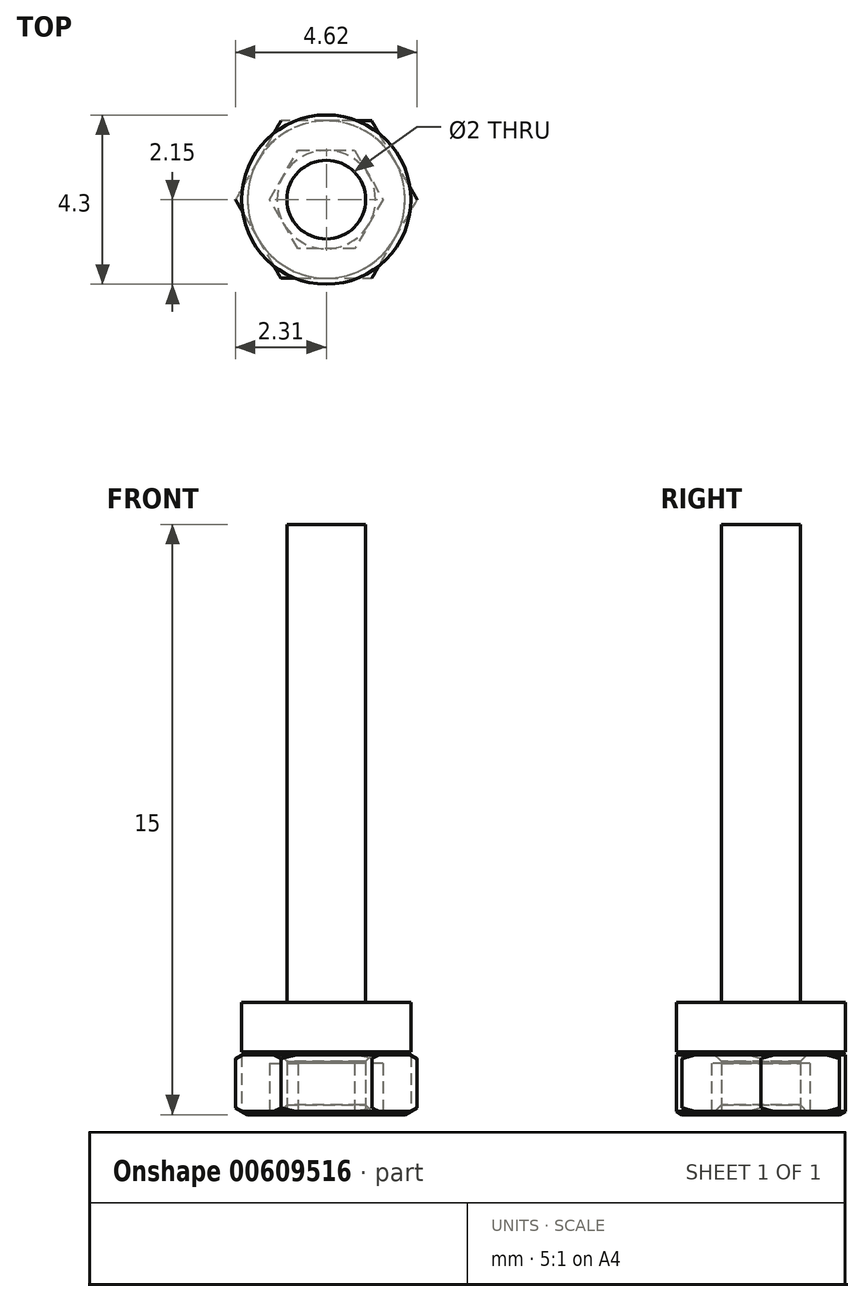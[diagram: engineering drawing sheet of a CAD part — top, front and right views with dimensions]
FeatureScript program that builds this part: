
annotation { "Feature Type Name" : "Feature", "Feature Type Description" : "" }
export const myFeature = defineFeature(function(context is Context, id is Id, definition is map)
    precondition{}
    {
        {
            var Q0;
            Q0=qCreatedBy(makeId("Top.planeOp"),FACE);
            var sketch = newSketch(context, id + "F0", { "sketchPlane" : qUnion([Q0])});
            skCircle(sketch, "E0", {"center": v(0, 0) * mm, "radius": 2.15 * mm});
            skCircle(sketch, "E1", {"center": v(0, 0) * mm, "radius": 1 * mm});
            skSolve(sketch);
        }
        {
            var Q0;
            Q0=makeQuery(id+"F0.imprint","IMPRINT",FACE,{"disambiguationData":[TD([[makeQuery(id+"F0.imprint","IMPRINT",EDGE,{"derivedFrom":sQuery(id+"F0.wireOp",EDGE,"E1")}),1.0]])]});
            var Q1;
            Q1=makeQuery(id+"F0.imprint","IMPRINT",FACE,{"disambiguationData":[TD([[makeQuery(id+"F0.imprint","IMPRINT",EDGE,{"derivedFrom":sQuery(id+"F0.wireOp",EDGE,"E0")}),1.0]])]});
            extrude(context, id + "F1", {"entities" : qUnion([Q0, Q1]), "depth" : 2.85 * mm});
        }
        {
            var Q0;
            Q0=makeQuery(id+"F0.imprint","IMPRINT",FACE,{"disambiguationData":[TD([[makeQuery(id+"F0.imprint","IMPRINT",EDGE,{"derivedFrom":sQuery(id+"F0.wireOp",EDGE,"E1")}),1.0]])]});
            extrude(context, id + "F2", {"entities" : qUnion([Q0]), "operationType" : NewBodyOperationType.ADD, "depth" : 15 * mm});
        }
        {
            var Q0;
            Q0=makeQuery(id+"F0.imprint","IMPRINT",FACE,{"disambiguationData":[TD([[makeQuery(id+"F0.imprint","IMPRINT",EDGE,{"derivedFrom":sQuery(id+"F0.wireOp",EDGE,"E0")}),1.0]])]});
            var sketch = newSketch(context, id + "F3", { "sketchPlane" : qUnion([Q0])});
            skCircle(sketch, "E2.cCircle", {"center": v(0, 0) * mm, "radius": 1.25 * mm, "construction": true});
            skLineSegment(sketch, "E2.0", {"start": v(0.72, -1.25) * mm, "end": v(-0.72, -1.25) * mm});
            skLineSegment(sketch, "E2.1", {"start": v(-0.72, -1.25) * mm, "end": v(-1.44, 0) * mm});
            skLineSegment(sketch, "E2.2", {"start": v(-1.44, 0) * mm, "end": v(-0.72, 1.25) * mm});
            skLineSegment(sketch, "E2.3", {"start": v(-0.72, 1.25) * mm, "end": v(0.72, 1.25) * mm});
            skLineSegment(sketch, "E2.4", {"start": v(0.72, 1.25) * mm, "end": v(1.44, 0) * mm});
            skLineSegment(sketch, "E2.5", {"start": v(1.44, 0) * mm, "end": v(0.72, -1.25) * mm});
            skPoint(sketch, "E2.0.midPoint", {"position": v(0, -1.25) * mm});
            skSolve(sketch);
        }
        {
            var Q0;
            Q0=makeQuery(id+"F3.imprint","IMPRINT",FACE,{"disambiguationData":[TD([[makeQuery(id+"F3.imprint","IMPRINT",EDGE,{"derivedFrom":sQuery(id+"F3.wireOp",EDGE,"E2.0")}),-1.0]])]});
            extrude(context, id + "F4", {"entities" : qUnion([Q0]), "operationType" : NewBodyOperationType.REMOVE, "depth" : 1.3 * mm});
        }
        {
            var Q0;
            Q0=qCreatedBy(makeId("Top.planeOp"),FACE);
            var sketch = newSketch(context, id + "F5", { "sketchPlane" : qUnion([Q0])});
            skCircle(sketch, "E3", {"center": v(0, 0) * mm, "radius": 1 * mm});
            skLineSegment(sketch, "E4.0", {"start": v(2, 1.06) * mm, "end": v(2, -1.06) * mm});
            skPoint(sketch, "E4.0.midPoint", {"position": v(2, 0) * mm});
            skCircle(sketch, "E5.cCircle", {"center": v(0, 0) * mm, "radius": 2 * mm, "construction": true});
            skLineSegment(sketch, "E5.0", {"start": v(2, 1.15) * mm, "end": v(2, -1.15) * mm});
            skLineSegment(sketch, "E5.1", {"start": v(2, -1.15) * mm, "end": v(0, -2.3) * mm});
            skLineSegment(sketch, "E5.2", {"start": v(0, -2.3) * mm, "end": v(-2, -1.15) * mm});
            skLineSegment(sketch, "E5.3", {"start": v(-2, -1.15) * mm, "end": v(-2, 1.15) * mm});
            skLineSegment(sketch, "E5.4", {"start": v(-2, 1.15) * mm, "end": v(0, 2.3) * mm});
            skLineSegment(sketch, "E5.5", {"start": v(0, 2.3) * mm, "end": v(2, 1.15) * mm});
            skSolve(sketch);
        }
        {
            var Q0;
            Q0=makeQuery(id+"F5.imprint","IMPRINT",FACE,{"disambiguationData":[TD([[makeQuery(id+"F5.imprint","IMPRINT",EDGE,{"derivedFrom":sQuery(id+"F5.wireOp",EDGE,"E3")}),-1.0]])]});
            extrude(context, id + "F6", {"entities" : qUnion([Q0]), "depth" : 1.6 * mm, "offsetDistance" : 25 * mm});
        }
        {
            var Q0;
            Q0=qCreatedBy(makeId("Front.planeOp"),FACE);
            var sketch = newSketch(context, id + "F7", { "sketchPlane" : qUnion([Q0])});
            skLineSegment(sketch, "E6", {"start": v(0, 0) * mm, "end": v(0, 1.6) * mm, "construction": true});
            skLineSegment(sketch, "E7", {"start": v(0, 0.8) * mm, "end": v(3.39, 0.8) * mm, "construction": true});
            skPoint(sketch, "E7.endSnap0", {"position": v(0, 0.8) * mm});
            skLineSegment(sketch, "E8", {"start": v(2, 1.6) * mm, "end": v(3.39, 1.6) * mm});
            skLineSegment(sketch, "E9", {"start": v(3.39, 1.6) * mm, "end": v(3.39, 0.8) * mm});
            skLineSegment(sketch, "E10", {"start": v(3.39, 0.8) * mm, "end": v(2, 1.6) * mm});
            skLineSegment(sketch, "E11.MirrorCS", {"start": v(2, 0) * mm, "end": v(3.39, 0) * mm});
            skLineSegment(sketch, "E12.MirrorCS", {"start": v(3.39, 0) * mm, "end": v(3.39, 0.8) * mm});
            skLineSegment(sketch, "E13.MirrorCS", {"start": v(3.39, 0.8) * mm, "end": v(2, 0) * mm});
            skSolve(sketch);
        }
        {
            var Q0;
            Q0=makeQuery(id+"F7.imprint","IMPRINT",FACE,{"disambiguationData":[TD([[makeQuery(id+"F7.imprint","IMPRINT",EDGE,{"derivedFrom":sQuery(id+"F7.wireOp",EDGE,"E8")}),-1.0]])]});
            var Q1;
            Q1=makeQuery(id+"F7.imprint","IMPRINT",FACE,{"disambiguationData":[TD([[makeQuery(id+"F7.imprint","IMPRINT",EDGE,{"derivedFrom":sQuery(id+"F7.wireOp",EDGE,"E11.MirrorCS")}),1.0]])]});
            var Q2;
            Q2=sQuery(id+"F7.wireOp",EDGE,"E6");
            revolve(context, id + "F8", {"operationType" : NewBodyOperationType.REMOVE, "entities" : qUnion([Q0, Q1]), "axis" : qUnion([Q2]), "revolveType" : RevolveType.FULL, "oppositeDirection" : true});
        }
        {
            var Q0;
            Q0=makeQuery(id+"F6.opExtrude","SWEPT_FACE",FACE,{"disambiguationData":[OSD([sQuery(id+"F5.wireOp",EDGE,"E3")])]});
            chamfer(context, id + "F9", {"entities" : qUnion([Q0]), "width" : 0.25 * mm, "tangentPropagation" : true});
        }
        {
            var Q0;
            Q0=makeQuery(id+"F6.opExtrude","SWEPT_BODY",BODY,{"disambiguationData":[OSD([sQuery(id+"F5.wireOp",EDGE,"E3"),sQuery(id+"F5.wireOp",EDGE,"E4.0"),sQuery(id+"F5.wireOp",EDGE,"E4.1"),sQuery(id+"F5.wireOp",EDGE,"E4.2"),sQuery(id+"F5.wireOp",EDGE,"E4.3"),sQuery(id+"F5.wireOp",EDGE,"E4.4"),sQuery(id+"F5.wireOp",EDGE,"E4.5")])]});
            var Q1;
            Q1=sQuery(id+"F7.wireOp",EDGE,"E6");
            transform(context, id + "F10", {"entities" : qUnion([Q0]), "transformType" : TransformType.ROTATION, "transformAxis" : qUnion([Q1]), "angle" : 30 * degree, "makeCopy" : false});
        }
    });
